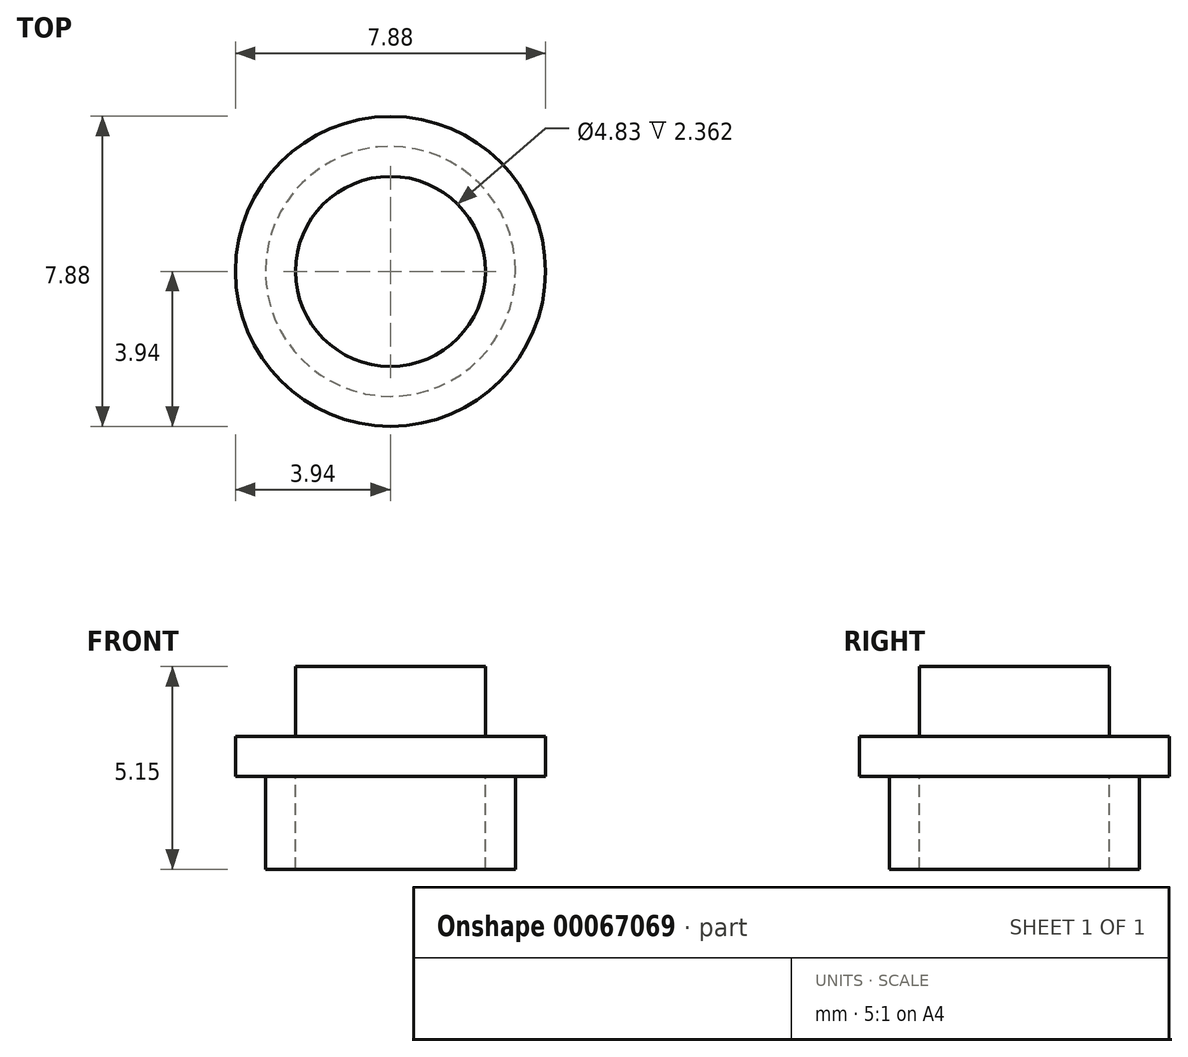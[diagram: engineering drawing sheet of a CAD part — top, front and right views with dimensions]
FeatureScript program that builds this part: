
annotation { "Feature Type Name" : "Feature", "Feature Type Description" : "" }
export const myFeature = defineFeature(function(context is Context, id is Id, definition is map)
    precondition{}
    {
        {
            var Q0;
            Q0=qCreatedBy(makeId("Top.planeOp"),FACE);
            var sketch = newSketch(context, id + "F0", { "sketchPlane" : qUnion([Q0])});
            skCircle(sketch, "E0", {"center": v(0, 0) * mm, "radius": 3.94 * mm});
            skSolve(sketch);
        }
        {
            var Q0;
            Q0=makeQuery(id+"F0.imprint","IMPRINT",FACE,{"disambiguationData":[TD([[makeQuery(id+"F0.imprint","IMPRINT",EDGE,{"derivedFrom":sQuery(id+"F0.wireOp",EDGE,"E0")}),1.0]])]});
            extrude(context, id + "F1", {"entities" : qUnion([Q0]), "depth" : 1.02 * mm});
        }
        {
            var Q0;
            Q0=makeQuery(id+"F1.opExtrude","CAP_FACE",FACE,{"disambiguationData":[OSD([sQuery(id+"F0.wireOp",EDGE,"E0")])],"isStart":false});
            var sketch = newSketch(context, id + "F2", { "sketchPlane" : qUnion([Q0])});
            skCircle(sketch, "E1", {"center": v(0, 0) * mm, "radius": 2.41 * mm});
            skSolve(sketch);
        }
        {
            var Q0;
            Q0=makeQuery(id+"F2.imprint","IMPRINT",FACE,{"disambiguationData":[TD([[makeQuery(id+"F2.imprint","IMPRINT",EDGE,{"derivedFrom":sQuery(id+"F2.wireOp",EDGE,"E1")}),1.0]])]});
            extrude(context, id + "F3", {"entities" : qUnion([Q0]), "operationType" : NewBodyOperationType.ADD, "depth" : 1.78 * mm});
        }
        {
            var Q0;
            Q0=makeQuery(id+"F1.opExtrude","CAP_FACE",FACE,{"disambiguationData":[OSD([sQuery(id+"F0.wireOp",EDGE,"E0")])],"isStart":true});
            var sketch = newSketch(context, id + "F4", { "sketchPlane" : qUnion([Q0])});
            skCircle(sketch, "E2", {"center": v(0, 0) * mm, "radius": 3.18 * mm});
            skCircle(sketch, "E3", {"center": v(0, 0) * mm, "radius": 2.41 * mm});
            skSolve(sketch);
        }
        {
            var Q0;
            Q0=makeQuery(id+"F4.imprint","IMPRINT",FACE,{"disambiguationData":[TD([[makeQuery(id+"F4.imprint","IMPRINT",EDGE,{"derivedFrom":sQuery(id+"F4.wireOp",EDGE,"E2")}),1.0]])]});
            extrude(context, id + "F5", {"entities" : qUnion([Q0]), "operationType" : NewBodyOperationType.ADD, "depth" : 2.36 * mm});
        }
    });
